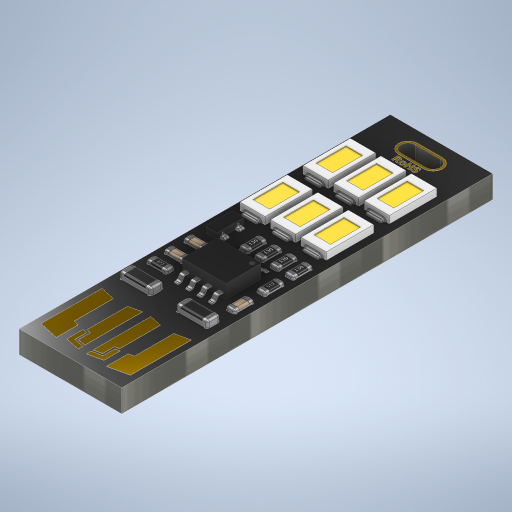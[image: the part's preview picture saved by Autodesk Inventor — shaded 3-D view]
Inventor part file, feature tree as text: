
AUTODESK INVENTOR PART (.ipt)
format: ipt  version: 2024 (Build 280153000, 153)  size: 5,328,896 bytes
history: native  units: mm
features: other x31, extrude x27, move_body x13, sketch x12, fillet x12, projected_geometry x10, plane x1, mirror x1
ambient origin geometry x8: Origin, YZ Plane, XZ Plane, XY Plane, X Axis, Y Axis, Z Axis, Center Point
bodies: Solid1 (feature_tree), Solid2 (feature_tree), Solid3 (feature_tree), Solid4 (feature_tree), Solid5 (feature_tree), Solid6 (feature_tree), Solid7 (feature_tree), Solid1_1 (feature_tree), Solid1_2 (feature_tree), Solid1_3 (feature_tree), Solid1_4 (feature_tree), Solid1_5 (feature_tree), Solid1_6 (feature_tree), Solid1_7 (feature_tree), Solid1_8 (feature_tree), Solid1_9 (feature_tree), Solid1_10 (feature_tree), Solid1_11 (feature_tree), Solid1_12 (feature_tree), Solid1_13 (feature_tree)
feature tree (107):
  other  "Transistor_3-leg.ipt"
  other  "MicroResistor.ipt"
  other  "MicroResistor_noPrint.ipt"
  other  "8-PinRectangleChip.ipt"
  other  "MicroResistor-LittleLarger.ipt"
  extrude  "Extrusion1"  Depth=42.62mm
  sketch  "Sketch2"  dims[d2=4.57mm d3=1.68mm]
  extrude  "Extrusion2"  Depth=1.68mm
  extrude  "Extrusion3"  Depth=2.58mm TaperAngle=0.0deg
  extrude  "Extrusion4"  Depth=5.45mm
  extrude  "Extrusion5"  Depth=5.5mm
  extrude  "Extrusion6"  Depth=2.91mm
  extrude  "Extrusion7"  Depth=2.91mm
  sketch  "Sketch3"  dims[d4=1.56mm d5=2.58mm d6=0.0mm]
  extrude  "Extrusion8"  Depth=0.6mm
  extrude  "Extrusion9"  Depth=0.85mm TaperAngle=0.0deg
  extrude  "Extrusion10"  Depth=0.85mm TaperAngle=0.0deg
  extrude  "Extrusion11"  Depth=0.85mm TaperAngle=0.0deg
  extrude  "Extrusion12"  Depth=1.85mm
  extrude  "Extrusion13"  Depth=0.45mm
  fillet  "Fillet1"  Radius=1.85mm
  fillet  "Fillet2"  Radius=1.85mm
  fillet  "Fillet3"  Radius=1.85mm
  fillet  "Fillet4"  Radius=1.85mm
  fillet  "Fillet5"  Radius=1.85mm
  fillet  "Fillet6"  Radius=1.85mm
  fillet  "Fillet7"  Radius=1.85mm
  fillet  "Fillet8"  Radius=1.85mm
  fillet  "Fillet9"  Radius=1.85mm
  fillet  "Fillet10"  Radius=1.85mm
  fillet  "Fillet11"  Radius=1.85mm
  fillet  "Fillet12"  Radius=0.25mm
  sketch  "Sketch4"  dims[d7=2.91mm d8=5.45mm]
  extrude  "Extrusion14"  Depth=0.25mm TaperAngle=0.0deg
  extrude  "Extrusion15"  Depth=0.25mm TaperAngle=0.0deg
  extrude  "Extrusion16"  Depth=0.25mm TaperAngle=0.0deg
  extrude  "Extrusion17"  Depth=0.25mm TaperAngle=0.0deg
  extrude  "Extrusion18"  Depth=0.25mm TaperAngle=0.0deg
  extrude  "Extrusion19"  Depth=0.2mm
  move_body  "Move Body1"
  move_body  "Move Body2"
  move_body  "Move Body3"
  move_body  "Move Body4"
  move_body  "Move Body5"
  move_body  "Move Body6"
  move_body  "Move Body7"
  move_body  "Move Body8"
  extrude  "Extrusion20"  Depth=0.2mm
  extrude  "Extrusion21"  Depth=0.2mm
  move_body  "Move Body9"
  extrude  "Extrusion22"  Depth=0.2mm
  move_body  "Move Body10"
  move_body  "Move Body11"
  extrude  "Extrusion23"  Depth=0.2mm
  extrude  "Extrusion24"  Depth=0.2mm
  move_body  "Move Body12"
  move_body  "Move Body13"
  extrude  "Extrusion25"  Depth=0.2mm
  plane  "Work Plane1"
  mirror  "Mirror1"
  extrude  "Extrusion26"  Depth=0.2mm
  extrude  "Extrusion27"  Depth=0.2mm
  sketch  "Sketch1"  dims[d0=11.76mm d1=42.62mm]
  other  "Solid1::Transistor_3-leg.ipt"
  other  "TaggingFeature1"
  other  "Solid1::MicroResistor.ipt"
  other  "TaggingFeature2"
  other  "Solid1::MicroResistor.ipt_1"
  other  "TaggingFeature3"
  other  "Solid1::MicroResistor.ipt_2"
  other  "TaggingFeature4"
  other  "Solid1::MicroResistor.ipt_3"
  other  "TaggingFeature5"
  other  "Solid1::MicroResistor.ipt_4"
  other  "TaggingFeature6"
  other  "Solid1::MicroResistor_noPrint.ipt"
  other  "TaggingFeature7"
  other  "Solid1::MicroResistor_noPrint.ipt_1"
  other  "TaggingFeature8"
  sketch  "Sketch5"  dims[d9=0.91mm d10=5.5mm]
  projected_geometry  "Projected Loop1"
  projected_geometry  "Projected Loop2"
  projected_geometry  "Projected Loop3"
  sketch  "Sketch6"  dims[d11=2.91mm d12=5.45mm d13=2.91mm d14=5.45mm]
  other  "Solid1::MicroResistor_noPrint.ipt_2"
  other  "TaggingFeature9"
  sketch  "Sketch7"  dims[d15=2.91mm d16=5.45mm d17=2.91mm d18=5.45mm]
  other  "Solid1::8-PinRectangleChip.ipt"
  other  "TaggingFeature10"
  other  "Solid1::MicroResistor.ipt_5"
  other  "TaggingFeature11"
  sketch  "Sketch8"  dims[d19=2.91mm d20=5.45mm d21=0.6mm d22=0.6mm]
  projected_geometry  "Projected Loop4"
  projected_geometry  "Projected Loop5"
  projected_geometry  "Projected Loop6"
  sketch  "Sketch9"  dims[d23=1.8mm d24=0.85mm d25=0.0mm]
  other  "Solid1::MicroResistor-LittleLarger.ipt"
  other  "TaggingFeature12"
  other  "Solid1::MicroResistor-LittleLarger.ipt_1"
  other  "TaggingFeature13"
  sketch  "Sketch10"  dims[d26=0.85mm d27=0.0mm d28=0.85mm d29=0.0mm]
  sketch  "Sketch11"  dims[d30=0.85mm d31=0.0mm d32=0.85mm d33=0.0mm]
  projected_geometry  "Projected Loop7"
  projected_geometry  "Projected Loop8"
  projected_geometry  "Projected Loop9"
  projected_geometry  "Projected Loop10"
  sketch  "Sketch12"  dims[d34=0.85mm d35=0.0mm d36=1.85mm d37=0.45mm d38=1.85mm d39=0.45mm d40=1.85mm d41=0.45mm d42=1.85mm d43=0.45mm d44=1.85mm d45=0.45mm d46=1.85mm d47=0.45mm d48=1.85mm d49=0.45mm d50=1.85mm d51=0.45mm d52=1.85mm d53=0.45mm d54=1.85mm d55=0.45mm d56=1.85mm d57=0.45mm d58=1.85mm d59=0.45mm d60=0.25mm d61=0.0mm d62=0.25mm d63=0.0mm d64=0.25mm d65=0.0mm d66=0.25mm d67=0.0mm d68=0.25mm d69=0.0mm d70=0.25mm d71=0.0mm d72=0.2mm d73=0.2mm d74=0.2mm d75=0.2mm d76=0.2mm d77=0.2mm d78=0.2mm d79=0.2mm d80=0.2mm d81=0.2mm d82=0.2mm d83=0.2mm d84=0.5mm d85=0.5mm d86=1.0mm d87=1.0mm d88=1.0mm d89=1.0mm d90=0.5mm d91=0.5mm d92=0.5mm d93=0.5mm d94=0.1mm d95=0.0mm d96=0.1mm d97=0.0mm d98=0.1mm d99=0.0mm d100=0.1mm d101=0.0mm d102=0.1mm d103=0.0mm d104=0.1mm d105=0.0mm d106=10.0mm d107=2.58mm d108=1.25mm d109=20.2mm d110=10.0mm d111=90.0deg d112=2.58mm d113=5.5mm d114=20.75mm d115=10.0mm d116=90.0deg d117=2.58mm d118=7.25mm d119=20.75mm d120=10.0mm d121=90.0deg d122=2.58mm d123=9.0mm d124=20.75mm d125=10.0mm d126=90.0deg d127=2.58mm d128=10.75mm d129=20.75mm d130=10.0mm d131=90.0deg d132=2.58mm d133=10.75mm d134=17.5mm d135=10.0mm d136=90.0deg d137=2.58mm d138=10.75mm d139=14.0mm d140=10.0mm d141=2.58mm d142=1.0mm d143=18.25mm d144=0.1mm d145=0.0mm d146=0.02mm d147=0.0mm d148=10.0mm d149=2.58mm d150=1.0mm d151=16.0mm d152=0.25mm d153=0.1mm d154=3.25mm d155=0.9mm d156=0.02mm d157=0.0mm d158=10.0mm d159=2.58mm d160=4.0mm d161=14.75mm d162=10.0mm d163=2.58mm d164=1.0mm d165=14.0mm d166=0.02mm d167=0.0mm d168=0.375mm d169=0.85mm d170=0.02mm d171=0.0mm d172=10.0mm d173=2.58mm d174=1.25mm d175=10.75mm d176=10.0mm d177=2.58mm d178=7.75mm d179=10.75mm d180=1.65mm d181=2.25mm d182=0.75mm d184=1.0mm d185=1.4mm d186=0.25mm d187=0.25mm d188=0.25mm d189=1.25mm d190=1.35mm d191=0.5mm d192=0.5mm d193=2.5mm d194=7.0mm d195=1.75mm d196=0.75mm d197=13.526302mm d198=0.02mm d199=0.0mm d200=0.02mm d201=0.0mm d202=11.0mm d203=1.333664mm d204=1.333664mm d205=10.824624mm d206=10.824624mm d207=20.231237mm d208=20.266721mm d209=1.333664mm d210=2.0mm d211=0.561598mm d212=0.85mm d213=0.2mm d214=0.2mm d215=0.02mm d216=0.0mm]
